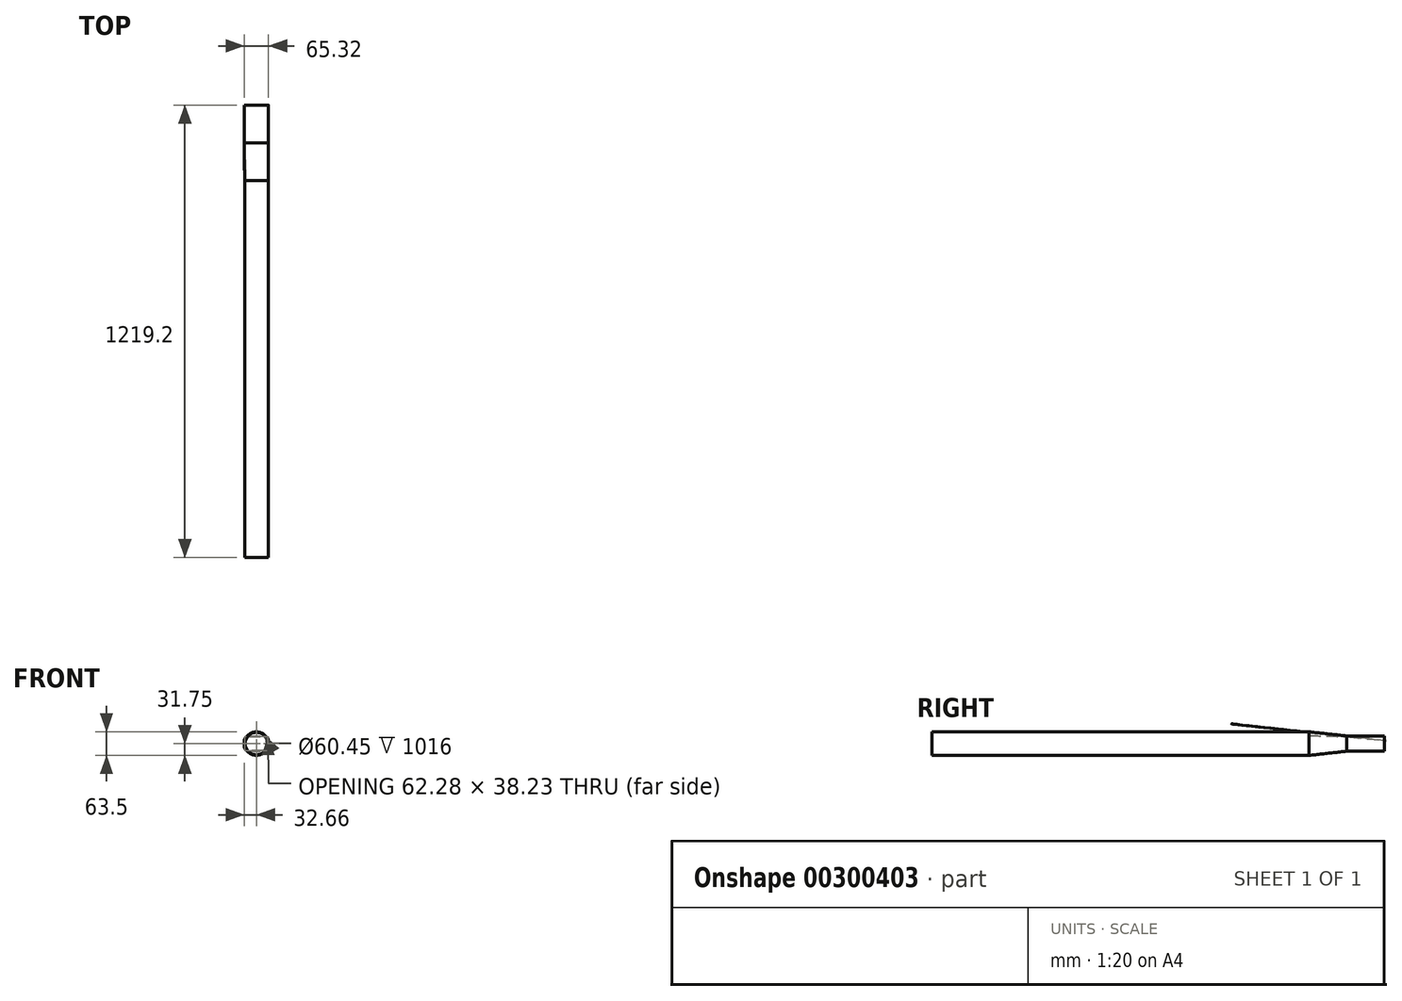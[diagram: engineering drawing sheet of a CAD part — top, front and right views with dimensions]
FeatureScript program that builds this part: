
annotation { "Feature Type Name" : "Feature", "Feature Type Description" : "" }
export const myFeature = defineFeature(function(context is Context, id is Id, definition is map)
    precondition{}
    {
        {
            var Q0;
            Q0=qCreatedBy(makeId("Front.planeOp"),FACE);
            cPlane(context, id + "F0", {"entities" : qUnion([Q0]), "cplaneType" : CPlaneType.OFFSET, "offset" : 101.6 * mm, "oppositeDirection" : true, "width" : 152.4 * mm, "height" : 152.4 * mm});
        }
        {
            var Q0;
            Q0=qCreatedBy(id+"F0.planeOp",FACE);
            var sketch = newSketch(context, id + "F1", { "sketchPlane" : qUnion([Q0])});
            skLineSegment(sketch, "E0.bottom", {"start": v(-19.84, 20.64) * mm, "end": v(19.84, 20.64) * mm});
            skLineSegment(sketch, "E0.top", {"start": v(-19.84, -20.64) * mm, "end": v(19.84, -20.64) * mm});
            skLineSegment(sketch, "E0.left", {"start": v(-32.66, 7.81) * mm, "end": v(-32.66, -7.81) * mm});
            skLineSegment(sketch, "E0.right", {"start": v(32.66, 7.81) * mm, "end": v(32.66, -7.81) * mm});
            skPoint(sketch, "E0.middle", {"position": v(0, 0) * mm});
            skPoint(sketch, "E1.visualSharp", {"position": v(32.66, 20.64) * mm});
            skArc(sketch, "E1.filletArc", {"start": v(32.66, 7.81) * mm, "mid": v(28.9, 16.88) * mm, "end": v(19.84, 20.64) * mm});
            skPoint(sketch, "E2.visualSharp", {"position": v(31.14, 19.11) * mm});
            skPoint(sketch, "E3.visualSharp", {"position": v(32.66, -20.64) * mm});
            skArc(sketch, "E3.filletArc", {"start": v(19.84, -20.64) * mm, "mid": v(28.9, -16.88) * mm, "end": v(32.66, -7.81) * mm});
            skPoint(sketch, "E4.visualSharp", {"position": v(31.14, -19.11) * mm});
            skPoint(sketch, "E5.visualSharp", {"position": v(-31.14, -19.11) * mm});
            skPoint(sketch, "E6.visualSharp", {"position": v(-32.66, -20.64) * mm});
            skArc(sketch, "E6.filletArc", {"start": v(-32.66, -7.81) * mm, "mid": v(-28.9, -16.88) * mm, "end": v(-19.84, -20.64) * mm});
            skPoint(sketch, "E7.visualSharp", {"position": v(-31.14, 19.11) * mm});
            skPoint(sketch, "E8.visualSharp", {"position": v(-32.66, 20.64) * mm});
            skArc(sketch, "E8.filletArc", {"start": v(-19.84, 20.64) * mm, "mid": v(-28.9, 16.88) * mm, "end": v(-32.66, 7.81) * mm});
            skSolve(sketch);
        }
        {
            var Q0;
            Q0 = qSketchRegion(id + "F1", true);
            extrude(context, id + "F2", {"entities" : qUnion([Q0]), "depth" : 101.6 * mm});
        }
        {
            var Q0;
            Q0=qCreatedBy(makeId("Front.planeOp"),FACE);
            cPlane(context, id + "F3", {"entities" : qUnion([Q0]), "cplaneType" : CPlaneType.OFFSET, "offset" : 101.6 * mm, "width" : 152.4 * mm, "height" : 152.4 * mm});
        }
        {
            var Q0;
            Q0=qCreatedBy(id+"F3.planeOp",FACE);
            var sketch = newSketch(context, id + "F4", { "sketchPlane" : qUnion([Q0])});
            skCircle(sketch, "E9", {"center": v(0, 0) * mm, "radius": 31.75 * mm});
            skSolve(sketch);
        }
        {
            var Q0;
            Q0 = qSketchRegion(id + "F4", true);
            extrude(context, id + "F5", {"entities" : qUnion([Q0]), "depth" : 1016 * mm});
        }
        {
            var Q0;
            Q0=makeQuery(id+"F5.opExtrude","CAP_FACE",FACE,{"disambiguationData":[OSD([sQuery(id+"F4.wireOp",EDGE,"E9")])],"isStart":true});
            var Q1;
            Q1=makeQuery(id+"F2.opExtrude","CAP_FACE",FACE,{"disambiguationData":[OSD([sQuery(id+"F1.wireOp",EDGE,"E0.bottom"),sQuery(id+"F1.wireOp",EDGE,"E0.top"),sQuery(id+"F1.wireOp",EDGE,"E0.left"),sQuery(id+"F1.wireOp",EDGE,"E0.right"),sQuery(id+"F1.wireOp",EDGE,"E1.filletArc"),sQuery(id+"F1.wireOp",EDGE,"E3.filletArc"),sQuery(id+"F1.wireOp",EDGE,"E6.filletArc"),sQuery(id+"F1.wireOp",EDGE,"E8.filletArc")])],"isStart":false});
            loft(context, id + "F6", {"sheetProfilesArray" : [{ "sheetProfileEntities" : qUnion([Q0]) }, { "sheetProfileEntities" : qUnion([Q1]) }]});
        }
        {
            var Q0;
            Q0=makeQuery(id+"F5.opExtrude","CAP_FACE",FACE,{"disambiguationData":[OSD([sQuery(id+"F4.wireOp",EDGE,"E9")])],"isStart":false});
            var Q1;
            Q1=makeQuery(id+"F5.opExtrude","CAP_FACE",FACE,{"disambiguationData":[OSD([sQuery(id+"F4.wireOp",EDGE,"E9")])],"isStart":true});
            shell(context, id + "F7", {"entities" : qUnion([Q0, Q1]), "thickness" : 1.52 * mm});
        }
        {
            var Q0;
            Q0=makeQuery(id+"F2.opExtrude","CAP_FACE",FACE,{"disambiguationData":[OSD([sQuery(id+"F1.wireOp",EDGE,"E0.bottom"),sQuery(id+"F1.wireOp",EDGE,"E0.top"),sQuery(id+"F1.wireOp",EDGE,"E0.left"),sQuery(id+"F1.wireOp",EDGE,"E0.right"),sQuery(id+"F1.wireOp",EDGE,"E1.filletArc"),sQuery(id+"F1.wireOp",EDGE,"E3.filletArc"),sQuery(id+"F1.wireOp",EDGE,"E6.filletArc"),sQuery(id+"F1.wireOp",EDGE,"E8.filletArc")])],"isStart":true});
            var Q1;
            Q1=makeQuery(id+"F2.opExtrude","CAP_FACE",FACE,{"disambiguationData":[OSD([sQuery(id+"F1.wireOp",EDGE,"E0.bottom"),sQuery(id+"F1.wireOp",EDGE,"E0.top"),sQuery(id+"F1.wireOp",EDGE,"E0.left"),sQuery(id+"F1.wireOp",EDGE,"E0.right"),sQuery(id+"F1.wireOp",EDGE,"E1.filletArc"),sQuery(id+"F1.wireOp",EDGE,"E3.filletArc"),sQuery(id+"F1.wireOp",EDGE,"E6.filletArc"),sQuery(id+"F1.wireOp",EDGE,"E8.filletArc")])],"isStart":false});
            shell(context, id + "F8", {"entities" : qUnion([Q0, Q1]), "thickness" : 1.52 * mm});
        }
        {
            var Q0;
            Q0=makeQuery(id+"F6.opLoft","CAP_FACE",FACE,{"disambiguationData":[OSD([sQuery(id+"F1.wireOp",EDGE,"E0.bottom"),sQuery(id+"F1.wireOp",EDGE,"E0.top"),sQuery(id+"F1.wireOp",EDGE,"E0.left"),sQuery(id+"F1.wireOp",EDGE,"E0.right"),sQuery(id+"F1.wireOp",EDGE,"E1.filletArc"),sQuery(id+"F1.wireOp",EDGE,"E3.filletArc"),sQuery(id+"F1.wireOp",EDGE,"E6.filletArc"),sQuery(id+"F1.wireOp",EDGE,"E8.filletArc")])],"isStart":true});
            shell(context, id + "F9", {"entities" : qUnion([Q0]), "thickness" : 1.52 * mm});
        }
    });
